annotation { "Feature Type Name" : "Feature", "Feature Type Description" : "" }
export const myFeature = defineFeature(function(context is Context, id is Id, definition is map)
    precondition{}
    {
        {
            var Q0;
            Q0=qCreatedBy(makeId("Front.planeOp"),FACE);
            var sketch = newSketch(context, id + "F0", { "sketchPlane" : qUnion([Q0])});
            skLineSegment(sketch, "E0.bottom", {"start": v(-25.4, 12.7) * mm, "end": v(25.4, 12.7) * mm});
            skLineSegment(sketch, "E0.top", {"start": v(-25.4, 0) * mm, "end": v(25.4, 0) * mm});
            skLineSegment(sketch, "E0.left", {"start": v(-25.4, 12.7) * mm, "end": v(-25.4, 0) * mm});
            skLineSegment(sketch, "E0.right", {"start": v(25.4, 12.7) * mm, "end": v(25.4, 0) * mm});
            skLineSegment(sketch, "E1", {"start": v(-25.4, 12.7) * mm, "end": v(0, 19.05) * mm});
            skLineSegment(sketch, "E2", {"start": v(0, 19.05) * mm, "end": v(25.4, 12.7) * mm});
            skSolve(sketch);
        }
        {
            var Q0;
            Q0=makeQuery(id+"F0.imprint","IMPRINT",FACE,{"disambiguationData":[TD([[makeQuery(id+"F0.imprint","IMPRINT",EDGE,{"derivedFrom":sQuery(id+"F0.wireOp",EDGE,"E0.bottom")}),-1.0]])]});
            var Q1;
            Q1=makeQuery(id+"F0.imprint","IMPRINT",FACE,{"disambiguationData":[TD([[makeQuery(id+"F0.imprint","IMPRINT",EDGE,{"derivedFrom":sQuery(id+"F0.wireOp",EDGE,"E0.bottom")}),1.0]])]});
            extrude(context, id + "F1", {"entities" : qUnion([Q0, Q1]), "depth" : 57.15 * mm});
        }
        {
            var Q0;
            Q0=makeQuery(id+"F1.opExtrude","CAP_FACE",FACE,{"disambiguationData":[OSD([sQuery(id+"F0.wireOp",EDGE,"E0.top"),sQuery(id+"F0.wireOp",EDGE,"E0.left"),sQuery(id+"F0.wireOp",EDGE,"E0.right"),sQuery(id+"F0.wireOp",EDGE,"E1"),sQuery(id+"F0.wireOp",EDGE,"E2")])],"isStart":false});
            var sketch = newSketch(context, id + "F2", { "sketchPlane" : qUnion([Q0])});
            skLineSegment(sketch, "E3.bottom", {"start": v(-9.53, 0) * mm, "end": v(9.53, 0) * mm});
            skLineSegment(sketch, "E3.top", {"start": v(-9.53, 11.11) * mm, "end": v(9.52, 11.11) * mm});
            skLineSegment(sketch, "E3.left", {"start": v(-9.53, 0) * mm, "end": v(-9.53, 11.11) * mm});
            skLineSegment(sketch, "E3.right", {"start": v(9.53, 0) * mm, "end": v(9.52, 11.11) * mm});
            skLineSegment(sketch, "E4.bottom", {"start": v(-19.05, 0) * mm, "end": v(-15.88, 0) * mm});
            skLineSegment(sketch, "E4.top", {"start": v(-19.05, 6.35) * mm, "end": v(-15.88, 6.35) * mm});
            skLineSegment(sketch, "E4.left", {"start": v(-19.05, 0) * mm, "end": v(-19.05, 6.35) * mm});
            skLineSegment(sketch, "E4.right", {"start": v(-15.88, 0) * mm, "end": v(-15.88, 6.35) * mm});
            skSolve(sketch);
        }
        {
            var Q0;
            Q0=makeQuery(id+"F2.imprint","IMPRINT",FACE,{"disambiguationData":[TD([[makeQuery(id+"F2.imprint","IMPRINT",EDGE,{"derivedFrom":sQuery(id+"F2.wireOp",EDGE,"E3.bottom")}),1.0]])]});
            extrude(context, id + "F3", {"entities" : qUnion([Q0]), "operationType" : NewBodyOperationType.REMOVE, "oppositeDirection" : true, "depth" : 1.27 * mm});
        }
        {
            var Q0;
            Q0=makeQuery(id+"F3.boolean.opBoolean","COPY",FACE,{"derivedFrom":makeQuery(id+"F3.opExtrude","CAP_FACE",FACE,{"disambiguationData":[OSD([sQuery(id+"F2.wireOp",EDGE,"E3.bottom"),sQuery(id+"F2.wireOp",EDGE,"E3.top"),sQuery(id+"F2.wireOp",EDGE,"E3.left"),sQuery(id+"F2.wireOp",EDGE,"E3.right")])],"isStart":false})});
            var sketch = newSketch(context, id + "F4", { "sketchPlane" : qUnion([Q0])});
            skLineSegment(sketch, "E5", {"start": v(-8.5, 0) * mm, "end": v(-8.5, 10.1) * mm});
            skLineSegment(sketch, "E6", {"start": v(-8.5, 10.1) * mm, "end": v(-1.14, 10.1) * mm});
            skLineSegment(sketch, "E7", {"start": v(-1.14, 10.1) * mm, "end": v(-1.14, 0) * mm});
            skLineSegment(sketch, "E8", {"start": v(-1.14, 0) * mm, "end": v(-0.13, 0) * mm});
            skLineSegment(sketch, "E9", {"start": v(-0.13, 0) * mm, "end": v(-0.13, 11.11) * mm});
            skLineSegment(sketch, "E10", {"start": v(-8.5, 6.1) * mm, "end": v(-1.14, 6.1) * mm});
            skLineSegment(sketch, "E11", {"start": v(-8.5, 5.08) * mm, "end": v(-1.14, 5.08) * mm});
            skLineSegment(sketch, "E12", {"start": v(-8.5, 1.02) * mm, "end": v(-1.14, 1.02) * mm});
            skLineSegment(sketch, "E13", {"start": v(-1.14, 5.08) * mm, "end": v(-8.5, 1.02) * mm});
            skLineSegment(sketch, "E14", {"start": v(-2.2, 5.08) * mm, "end": v(-8.5, 1.6) * mm});
            skLineSegment(sketch, "E15", {"start": v(-1.14, 4.5) * mm, "end": v(-7.46, 1.02) * mm});
            skLineSegment(sketch, "E16", {"start": v(-0.13, 11.11) * mm, "end": v(-9.53, 11.11) * mm});
            skLineSegment(sketch, "E17", {"start": v(-9.53, 11.11) * mm, "end": v(-9.53, 0) * mm});
            skLineSegment(sketch, "E18", {"start": v(-9.53, 0) * mm, "end": v(-0.13, 0) * mm});
            skLineSegment(sketch, "E19.MirrorCS", {"start": v(1.14, 5.08) * mm, "end": v(8.5, 1.02) * mm});
            skLineSegment(sketch, "E20.MirrorCS", {"start": v(1.14, 10.1) * mm, "end": v(1.14, 0) * mm});
            skLineSegment(sketch, "E21.MirrorCS", {"start": v(8.5, 6.1) * mm, "end": v(1.14, 6.1) * mm});
            skLineSegment(sketch, "E22.MirrorCS", {"start": v(8.5, 5.08) * mm, "end": v(1.14, 5.08) * mm});
            skLineSegment(sketch, "E23.MirrorCS", {"start": v(2.2, 5.08) * mm, "end": v(8.5, 1.6) * mm});
            skLineSegment(sketch, "E24.MirrorCS", {"start": v(1.14, 4.5) * mm, "end": v(7.46, 1.02) * mm});
            skLineSegment(sketch, "E25.MirrorCS", {"start": v(8.5, 1.02) * mm, "end": v(1.14, 1.02) * mm});
            skLineSegment(sketch, "E26.MirrorCS", {"start": v(9.53, 0) * mm, "end": v(0.13, 0) * mm});
            skLineSegment(sketch, "E27.MirrorCS", {"start": v(8.5, 0) * mm, "end": v(8.5, 10.1) * mm});
            skLineSegment(sketch, "E28.MirrorCS", {"start": v(9.53, 11.11) * mm, "end": v(9.53, 0) * mm});
            skLineSegment(sketch, "E29.MirrorCS", {"start": v(8.5, 10.1) * mm, "end": v(1.14, 10.1) * mm});
            skLineSegment(sketch, "E30.MirrorCS", {"start": v(0.13, 11.11) * mm, "end": v(9.53, 11.11) * mm});
            skLineSegment(sketch, "E31.MirrorCS", {"start": v(0.13, 0) * mm, "end": v(0.13, 11.11) * mm});
            skSolve(sketch);
        }
        {
            var Q0;
            {var subQ9=sQuery(id+"F4.wireOp",EDGE,"E6");Q0=makeQuery(id+"F4.imprint","IMPRINT",FACE,{"disambiguationData":[TD([[makeQuery(id+"F4.imprint","IMPRINT",EDGE,{"derivedFrom":subQ9}),1.0]])]});}
            var Q1;
            {var subQ4=sQuery(id+"F4.wireOp",EDGE,"E10");Q1=makeQuery(id+"F4.imprint","IMPRINT",FACE,{"disambiguationData":[TD([[makeQuery(id+"F4.imprint","IMPRINT",EDGE,{"derivedFrom":subQ4}),-1.0]])]});}
            var Q2;
            {var subQ0=sQuery(id+"F4.wireOp",EDGE,"E13");Q2=makeQuery(id+"F4.imprint","IMPRINT",FACE,{"disambiguationData":[TD([[makeQuery(id+"F4.imprint","IMPRINT",EDGE,{"derivedFrom":subQ0}),-1.0]])]});}
            var Q3;
            {var subQ0=sQuery(id+"F4.wireOp",EDGE,"E13");Q3=makeQuery(id+"F4.imprint","IMPRINT",FACE,{"disambiguationData":[TD([[makeQuery(id+"F4.imprint","IMPRINT",EDGE,{"derivedFrom":subQ0}),1.0]])]});}
            var Q4;
            {var subQ1=sQuery(id+"F4.wireOp",EDGE,"E7");var subQ6=sQuery(id+"F4.wireOp",EDGE,"E18");var subQ8=makeQuery(id+"F4.imprint","INTERSECT",VERTEX,{"derivedFrom":[subQ1,subQ6]});Q4=makeQuery(id+"F4.imprint","IMPRINT",FACE,{"disambiguationData":[TD([[makeQuery(id+"F4.imprint","IMPRINT",EDGE,{"disambiguationData":[TD([[subQ8,1.0]])],"derivedFrom":subQ1}),-1.0]])]});}
            var Q5;
            {var subQ2=sQuery(id+"F4.wireOp",EDGE,"E20.MirrorCS");var subQ4=sQuery(id+"F4.wireOp",EDGE,"E26.MirrorCS");var subQ5=makeQuery(id+"F4.imprint","INTERSECT",VERTEX,{"derivedFrom":[subQ2,subQ4]});Q5=makeQuery(id+"F4.imprint","IMPRINT",FACE,{"disambiguationData":[TD([[makeQuery(id+"F4.imprint","IMPRINT",EDGE,{"disambiguationData":[TD([[subQ5,1.0]])],"derivedFrom":subQ2}),1.0]])]});}
            var Q6;
            {var subQ17=sQuery(id+"F4.wireOp",EDGE,"E28.MirrorCS");Q6=makeQuery(id+"F4.imprint","IMPRINT",FACE,{"disambiguationData":[TD([[makeQuery(id+"F4.imprint","IMPRINT",EDGE,{"derivedFrom":subQ17}),1.0]])]});}
            var Q7;
            {var subQ4=sQuery(id+"F4.wireOp",EDGE,"E21.MirrorCS");Q7=makeQuery(id+"F4.imprint","IMPRINT",FACE,{"disambiguationData":[TD([[makeQuery(id+"F4.imprint","IMPRINT",EDGE,{"derivedFrom":subQ4}),1.0]])]});}
            var Q8;
            {var subQ0=sQuery(id+"F4.wireOp",EDGE,"E19.MirrorCS");Q8=makeQuery(id+"F4.imprint","IMPRINT",FACE,{"disambiguationData":[TD([[makeQuery(id+"F4.imprint","IMPRINT",EDGE,{"derivedFrom":subQ0}),1.0]])]});}
            var Q9;
            {var subQ0=sQuery(id+"F4.wireOp",EDGE,"E19.MirrorCS");Q9=makeQuery(id+"F4.imprint","IMPRINT",FACE,{"disambiguationData":[TD([[makeQuery(id+"F4.imprint","IMPRINT",EDGE,{"derivedFrom":subQ0}),-1.0]])]});}
            extrude(context, id + "F5", {"entities" : qUnion([Q0, Q1, Q2, Q3, Q4, Q5, Q6, Q7, Q8, Q9]), "operationType" : NewBodyOperationType.ADD, "depth" : 0.64 * mm});
        }
        {
            var Q0;
            {var subQ0=sQuery(id+"F0.wireOp",EDGE,"E0.left");var subQ1=sQuery(id+"F0.wireOp",EDGE,"E1");var subQ2=sQuery(id+"F0.wireOp",EDGE,"E2");var subQ3=sQuery(id+"F0.wireOp",EDGE,"E0.right");var subQ4=sQuery(id+"F0.wireOp",EDGE,"E0.top");Q0=makeQuery(id+"FkIv4KLba7RXvQa_1.boolean.opBoolean","SPLIT",FACE,{"disambiguationData":[TD([makeQuery(id+"F1.opExtrude","SWEPT_FACE",FACE,{"disambiguationData":[OSD([subQ4])]})])],"derivedFrom":makeQuery(id+"F1.opExtrude","CAP_FACE",FACE,{"disambiguationData":[OSD([subQ4,subQ0,subQ3,subQ1,subQ2])],"isStart":false})});}
            var sketch = newSketch(context, id + "F6", { "sketchPlane" : qUnion([Q0])});
            skLineSegment(sketch, "E32.bottom", {"start": v(-19.05, 0) * mm, "end": v(-15.88, 0) * mm});
            skLineSegment(sketch, "E32.top", {"start": v(-19.05, 6.35) * mm, "end": v(-15.88, 6.35) * mm});
            skLineSegment(sketch, "E32.left", {"start": v(-19.05, 0) * mm, "end": v(-19.05, 6.35) * mm});
            skLineSegment(sketch, "E32.right", {"start": v(-15.88, 0) * mm, "end": v(-15.88, 6.35) * mm});
            skSolve(sketch);
        }
        {
            var Q0;
            Q0=makeQuery(id+"F6.imprint","IMPRINT",FACE,{"disambiguationData":[TD([[makeQuery(id+"F6.imprint","IMPRINT",EDGE,{"derivedFrom":sQuery(id+"F6.wireOp",EDGE,"E32.bottom")}),1.0]])]});
            extrude(context, id + "F7", {"entities" : qUnion([Q0]), "operationType" : NewBodyOperationType.REMOVE, "oppositeDirection" : true, "depth" : 0.5 * mm});
        }
        {
            var Q0;
            Q0=makeQuery(id+"F7.boolean.opBoolean","COPY",FACE,{"derivedFrom":makeQuery(id+"F7.opExtrude","CAP_FACE",FACE,{"disambiguationData":[OSD([sQuery(id+"F6.wireOp",EDGE,"E32.bottom"),sQuery(id+"F6.wireOp",EDGE,"E32.top"),sQuery(id+"F6.wireOp",EDGE,"E32.left"),sQuery(id+"F6.wireOp",EDGE,"E32.right")])],"isStart":false})});
            var sketch = newSketch(context, id + "F8", { "sketchPlane" : qUnion([Q0])});
            skCircle(sketch, "E33", {"center": v(-18.29, 3.18) * mm, "radius": 0.2 * mm});
            skSolve(sketch);
        }
        {
            var Q0;
            Q0=makeQuery(id+"F8.imprint","IMPRINT",FACE,{"disambiguationData":[TD([[makeQuery(id+"F8.imprint","IMPRINT",EDGE,{"derivedFrom":sQuery(id+"F8.wireOp",EDGE,"E33")}),1.0]])]});
            extrude(context, id + "F9", {"entities" : qUnion([Q0]), "operationType" : NewBodyOperationType.ADD, "depth" : 0.5 * mm});
        }
        {
            var Q0;
            Q0=makeQuery(id+"F1.opExtrude","SWEPT_FACE",FACE,{"disambiguationData":[OSD([sQuery(id+"F0.wireOp",EDGE,"E0.left")])]});
            var sketch = newSketch(context, id + "F10", { "sketchPlane" : qUnion([Q0])});
            skLineSegment(sketch, "E34.bottom", {"start": v(53.97, 9.52) * mm, "end": v(41.37, 9.52) * mm});
            skLineSegment(sketch, "E34.top", {"start": v(53.97, 2.54) * mm, "end": v(41.37, 2.54) * mm});
            skLineSegment(sketch, "E34.left", {"start": v(53.97, 9.52) * mm, "end": v(53.97, 2.54) * mm});
            skLineSegment(sketch, "E34.right", {"start": v(41.37, 9.52) * mm, "end": v(41.37, 2.54) * mm});
            skLineSegment(sketch, "E35.bottom", {"start": v(40.35, 9.53) * mm, "end": v(27.75, 9.53) * mm});
            skLineSegment(sketch, "E35.top", {"start": v(40.35, 2.54) * mm, "end": v(27.75, 2.54) * mm});
            skLineSegment(sketch, "E35.left", {"start": v(40.35, 9.53) * mm, "end": v(40.35, 2.54) * mm});
            skLineSegment(sketch, "E35.right", {"start": v(27.75, 9.53) * mm, "end": v(27.75, 2.54) * mm});
            skLineSegment(sketch, "E36.bottom", {"start": v(26.73, 9.52) * mm, "end": v(14.13, 9.52) * mm});
            skLineSegment(sketch, "E36.top", {"start": v(26.73, 2.54) * mm, "end": v(14.13, 2.54) * mm});
            skLineSegment(sketch, "E36.left", {"start": v(26.73, 9.53) * mm, "end": v(26.73, 2.54) * mm});
            skLineSegment(sketch, "E36.right", {"start": v(14.13, 9.53) * mm, "end": v(14.13, 2.54) * mm});
            skLineSegment(sketch, "E37.bottom", {"start": v(13.11, 9.52) * mm, "end": v(0.5, 9.52) * mm});
            skLineSegment(sketch, "E37.top", {"start": v(13.11, 2.54) * mm, "end": v(0.5, 2.54) * mm});
            skLineSegment(sketch, "E37.left", {"start": v(13.11, 9.52) * mm, "end": v(13.11, 2.54) * mm});
            skLineSegment(sketch, "E37.right", {"start": v(0.5, 9.52) * mm, "end": v(0.5, 2.54) * mm});
            skSolve(sketch);
        }
        {
            var Q0;
            Q0=makeQuery(id+"F10.imprint","IMPRINT",FACE,{"disambiguationData":[TD([[makeQuery(id+"F10.imprint","IMPRINT",EDGE,{"derivedFrom":sQuery(id+"F10.wireOp",EDGE,"727a1d76-4258-429a-ad4e-49e237d1b87a.bottom")}),1.0]])]});
            var Q1;
            Q1=makeQuery(id+"F10.imprint","IMPRINT",FACE,{"disambiguationData":[TD([[makeQuery(id+"F10.imprint","IMPRINT",EDGE,{"derivedFrom":sQuery(id+"F10.wireOp",EDGE,"fbcd54c6-16bd-4673-946f-ba1503210179.bottom")}),1.0]])]});
            var Q2;
            Q2=makeQuery(id+"F10.imprint","IMPRINT",FACE,{"disambiguationData":[TD([[makeQuery(id+"F10.imprint","IMPRINT",EDGE,{"derivedFrom":sQuery(id+"F10.wireOp",EDGE,"f456708e-a3c8-40d2-a44c-2f1cd61e3648.bottom")}),1.0]])]});
            var Q3;
            Q3=makeQuery(id+"F10.imprint","IMPRINT",FACE,{"disambiguationData":[TD([[makeQuery(id+"F10.imprint","IMPRINT",EDGE,{"derivedFrom":sQuery(id+"F10.wireOp",EDGE,"857afa44-62f5-48bd-8139-67d137270524.bottom")}),1.0]])]});
            var Q4;
            Q4=makeQuery(id+"F10.imprint","IMPRINT",FACE,{"disambiguationData":[TD([[makeQuery(id+"F10.imprint","IMPRINT",EDGE,{"derivedFrom":sQuery(id+"F10.wireOp",EDGE,"E37.bottom")}),1.0]])]});
            var Q5;
            Q5=makeQuery(id+"F10.imprint","IMPRINT",FACE,{"disambiguationData":[TD([[makeQuery(id+"F10.imprint","IMPRINT",EDGE,{"derivedFrom":sQuery(id+"F10.wireOp",EDGE,"E36.bottom")}),1.0]])]});
            var Q6;
            Q6=makeQuery(id+"F10.imprint","IMPRINT",FACE,{"disambiguationData":[TD([[makeQuery(id+"F10.imprint","IMPRINT",EDGE,{"derivedFrom":sQuery(id+"F10.wireOp",EDGE,"E35.bottom")}),1.0]])]});
            var Q7;
            Q7=makeQuery(id+"F10.imprint","IMPRINT",FACE,{"disambiguationData":[TD([[makeQuery(id+"F10.imprint","IMPRINT",EDGE,{"derivedFrom":sQuery(id+"F10.wireOp",EDGE,"E34.bottom")}),1.0]])]});
            extrude(context, id + "F11", {"entities" : qUnion([Q0, Q1, Q2, Q3, Q4, Q5, Q6, Q7]), "operationType" : NewBodyOperationType.REMOVE, "oppositeDirection" : true, "depth" : 0.38 * mm});
        }
        {
            var Q0;
            Q0=makeQuery(id+"F1.opExtrude","SWEPT_FACE",FACE,{"disambiguationData":[OSD([sQuery(id+"F0.wireOp",EDGE,"E0.right")])]});
            var sketch = newSketch(context, id + "F12", { "sketchPlane" : qUnion([Q0])});
            skLineSegment(sketch, "E38.bottom", {"start": v(-53.98, 9.53) * mm, "end": v(-41.37, 9.53) * mm});
            skLineSegment(sketch, "E38.top", {"start": v(-53.98, 2.54) * mm, "end": v(-41.37, 2.54) * mm});
            skLineSegment(sketch, "E38.left", {"start": v(-53.98, 9.53) * mm, "end": v(-53.98, 2.54) * mm});
            skLineSegment(sketch, "E38.right", {"start": v(-41.37, 9.53) * mm, "end": v(-41.37, 2.54) * mm});
            skLineSegment(sketch, "E39.bottom", {"start": v(-40.35, 9.53) * mm, "end": v(-27.75, 9.53) * mm});
            skLineSegment(sketch, "E39.top", {"start": v(-40.35, 2.54) * mm, "end": v(-27.75, 2.54) * mm});
            skLineSegment(sketch, "E39.left", {"start": v(-40.35, 9.53) * mm, "end": v(-40.35, 2.54) * mm});
            skLineSegment(sketch, "E39.right", {"start": v(-27.75, 9.53) * mm, "end": v(-27.75, 2.54) * mm});
            skLineSegment(sketch, "E40.bottom", {"start": v(-26.73, 9.53) * mm, "end": v(-14.13, 9.53) * mm});
            skLineSegment(sketch, "E40.top", {"start": v(-26.73, 2.54) * mm, "end": v(-14.13, 2.54) * mm});
            skLineSegment(sketch, "E40.left", {"start": v(-26.73, 9.53) * mm, "end": v(-26.73, 2.54) * mm});
            skLineSegment(sketch, "E40.right", {"start": v(-14.13, 9.53) * mm, "end": v(-14.13, 2.54) * mm});
            skLineSegment(sketch, "E41.bottom", {"start": v(-13.11, 9.53) * mm, "end": v(-0.5, 9.53) * mm});
            skLineSegment(sketch, "E41.top", {"start": v(-13.11, 2.54) * mm, "end": v(-0.5, 2.54) * mm});
            skLineSegment(sketch, "E41.left", {"start": v(-13.11, 9.53) * mm, "end": v(-13.11, 2.54) * mm});
            skLineSegment(sketch, "E41.right", {"start": v(-0.5, 9.53) * mm, "end": v(-0.5, 2.54) * mm});
            skSolve(sketch);
        }
        {
            var Q0;
            Q0=makeQuery(id+"F12.imprint","IMPRINT",FACE,{"disambiguationData":[TD([[makeQuery(id+"F12.imprint","IMPRINT",EDGE,{"derivedFrom":sQuery(id+"F12.wireOp",EDGE,"E38.bottom")}),-1.0]])]});
            var Q1;
            Q1=makeQuery(id+"F12.imprint","IMPRINT",FACE,{"disambiguationData":[TD([[makeQuery(id+"F12.imprint","IMPRINT",EDGE,{"derivedFrom":sQuery(id+"F12.wireOp",EDGE,"E39.bottom")}),-1.0]])]});
            var Q2;
            Q2=makeQuery(id+"F12.imprint","IMPRINT",FACE,{"disambiguationData":[TD([[makeQuery(id+"F12.imprint","IMPRINT",EDGE,{"derivedFrom":sQuery(id+"F12.wireOp",EDGE,"E40.bottom")}),-1.0]])]});
            var Q3;
            Q3=makeQuery(id+"F12.imprint","IMPRINT",FACE,{"disambiguationData":[TD([[makeQuery(id+"F12.imprint","IMPRINT",EDGE,{"derivedFrom":sQuery(id+"F12.wireOp",EDGE,"E41.bottom")}),-1.0]])]});
            var Q4;
            Q4=makeQuery(id+"F12.imprint","IMPRINT",FACE,{"disambiguationData":[TD([[makeQuery(id+"F12.imprint","IMPRINT",EDGE,{"derivedFrom":sQuery(id+"F12.wireOp",EDGE,"e12e58a7-e691-4093-903c-9c184ae4cd88.bottom")}),-1.0]])]});
            var Q5;
            Q5=makeQuery(id+"F12.imprint","IMPRINT",FACE,{"disambiguationData":[TD([[makeQuery(id+"F12.imprint","IMPRINT",EDGE,{"derivedFrom":sQuery(id+"F12.wireOp",EDGE,"4a9eed8a-eaee-461f-81b4-e3a02307e155.bottom")}),-1.0]])]});
            var Q6;
            Q6=makeQuery(id+"F12.imprint","IMPRINT",FACE,{"disambiguationData":[TD([[makeQuery(id+"F12.imprint","IMPRINT",EDGE,{"derivedFrom":sQuery(id+"F12.wireOp",EDGE,"bde78560-5837-450a-b62f-a72f43ab685d.bottom")}),-1.0]])]});
            var Q7;
            Q7=makeQuery(id+"F12.imprint","IMPRINT",FACE,{"disambiguationData":[TD([[makeQuery(id+"F12.imprint","IMPRINT",EDGE,{"derivedFrom":sQuery(id+"F12.wireOp",EDGE,"723e41c7-2ad6-4fed-aca1-4fab76280504.bottom")}),-1.0]])]});
            extrude(context, id + "F13", {"entities" : qUnion([Q0, Q1, Q2, Q3, Q4, Q5, Q6, Q7]), "operationType" : NewBodyOperationType.REMOVE, "oppositeDirection" : true, "depth" : 0.38 * mm});
        }
        {
            var Q0;
            Q0=makeQuery(id+"F1.opExtrude","SWEPT_BODY",BODY,{"disambiguationData":[OSD([sQuery(id+"F0.wireOp",EDGE,"E0.top"),sQuery(id+"F0.wireOp",EDGE,"E0.left"),sQuery(id+"F0.wireOp",EDGE,"E0.right"),sQuery(id+"F0.wireOp",EDGE,"E1"),sQuery(id+"F0.wireOp",EDGE,"E2")])]});
            var Q1;
            Q1=qCreatedBy(makeId("Front.planeOp"),FACE);
            mirror(context, id + "F14", {"operationType" : NewBodyOperationType.ADD, "entities" : qUnion([Q0]), "mirrorPlane" : qUnion([Q1])});
        }
        {
            var Q0;
            Q0=makeQuery(id+"F1.opExtrude","CAP_FACE",FACE,{"disambiguationData":[OSD([sQuery(id+"F0.wireOp",EDGE,"E0.top"),sQuery(id+"F0.wireOp",EDGE,"E0.left"),sQuery(id+"F0.wireOp",EDGE,"E0.right"),sQuery(id+"F0.wireOp",EDGE,"E1"),sQuery(id+"F0.wireOp",EDGE,"E2")])],"isStart":false});
            var sketch = newSketch(context, id + "F15", { "sketchPlane" : qUnion([Q0])});
            skText(sketch, "E42", { "text": "Achen Farms", "fontName": "OpenSans-Regular.ttf"});
            const initialGuessF15  = {"E42": [-0.01323, 0.01207, 1, 0, 0.00317]};
            skSetInitialGuess(sketch, initialGuessF15);
            skSolve(sketch);
        }
        {
            var Q0;
            Q0 = qSketchRegion(id + "F15", true);
            extrude(context, id + "F16", {"entities" : qUnion([Q0]), "operationType" : NewBodyOperationType.REMOVE, "oppositeDirection" : true, "depth" : 0.38 * mm});
        }
        {
            var Q0;
            Q0=makeQuery(id+"F14.opPattern","COPY",FACE,{"derivedFrom":makeQuery(id+"F1.opExtrude","CAP_FACE",FACE,{"disambiguationData":[OSD([sQuery(id+"F0.wireOp",EDGE,"E0.top"),sQuery(id+"F0.wireOp",EDGE,"E0.left"),sQuery(id+"F0.wireOp",EDGE,"E0.right"),sQuery(id+"F0.wireOp",EDGE,"E1"),sQuery(id+"F0.wireOp",EDGE,"E2")])],"isStart":false}),"instanceName":"1"});
            var sketch = newSketch(context, id + "F17", { "sketchPlane" : qUnion([Q0])});
            skText(sketch, "E43", { "text": "Achen Farms", "fontName": "OpenSans-Regular.ttf"});
            const initialGuessF17  = {"E43": [-0.01323, 0.01206, 1, 0, 0.00318]};
            skSetInitialGuess(sketch, initialGuessF17);
            skSolve(sketch);
        }
        {
            var Q0;
            Q0 = qSketchRegion(id + "F17", true);
            extrude(context, id + "F18", {"entities" : qUnion([Q0]), "operationType" : NewBodyOperationType.REMOVE, "oppositeDirection" : true, "depth" : 0.38 * mm});
        }
        {
            var Q0;
            {var subQ0=makeQuery(id+"F5.boolean.opBoolean","MERGE",FACE,{"derivedFrom":[makeQuery(id+"F1.opExtrude","SWEPT_FACE",FACE,{"disambiguationData":[OSD([sQuery(id+"F0.wireOp",EDGE,"E0.top")])]}),makeQuery(id+"F5.opExtrude","SWEPT_FACE",FACE,{"disambiguationData":[OSD([sQuery(id+"F4.wireOp",EDGE,"E18")])]}),makeQuery(id+"F5.opExtrude","SWEPT_FACE",FACE,{"disambiguationData":[OSD([sQuery(id+"F4.wireOp",EDGE,"E26.MirrorCS")])]})]});Q0=makeQuery(id+"F14.boolean.opBoolean","MERGE",FACE,{"derivedFrom":[subQ0,makeQuery(id+"F14.opPattern","COPY",FACE,{"derivedFrom":subQ0,"instanceName":"1"})]});}
            var sketch = newSketch(context, id + "F19", { "sketchPlane" : qUnion([Q0])});
            skLineSegment(sketch, "E44.bottom", {"start": v(-25.4, 57.15) * mm, "end": v(-36.51, 57.15) * mm});
            skLineSegment(sketch, "E44.top", {"start": v(-25.4, 47.63) * mm, "end": v(-36.51, 47.63) * mm});
            skLineSegment(sketch, "E44.left", {"start": v(-25.4, 57.15) * mm, "end": v(-25.4, 47.63) * mm});
            skLineSegment(sketch, "E44.right", {"start": v(-36.51, 57.15) * mm, "end": v(-36.51, 47.62) * mm});
            skSolve(sketch);
        }
        {
            var Q0;
            Q0=makeQuery(id+"F19.imprint","IMPRINT",FACE,{"disambiguationData":[TD([[makeQuery(id+"F19.imprint","IMPRINT",EDGE,{"derivedFrom":sQuery(id+"F19.wireOp",EDGE,"E44.bottom")}),1.0]])]});
            extrude(context, id + "F20", {"entities" : qUnion([Q0]), "operationType" : NewBodyOperationType.ADD, "oppositeDirection" : true, "depth" : 0.64 * mm});
        }
        {
            var Q0;
            {var subQ0=sQuery(id+"F0.wireOp",EDGE,"E0.right");var subQ4=sQuery(id+"F0.wireOp",EDGE,"E0.top");var subQ5=makeQuery(id+"F1.opExtrude","SWEPT_FACE",FACE,{"disambiguationData":[OSD([subQ4])]});var subQ6=sQuery(id+"F0.wireOp",EDGE,"E0.left");var subQ8=sQuery(id+"F0.wireOp",EDGE,"E1");var subQ10=sQuery(id+"F0.wireOp",EDGE,"E2");Q0=makeQuery(id+"F20.boolean.opBoolean","MERGE",FACE,{"derivedFrom":[makeQuery(id+"F16.boolean.opBoolean","SPLIT",FACE,{"disambiguationData":[TD([subQ5])],"derivedFrom":makeQuery(id+"F1.opExtrude","CAP_FACE",FACE,{"disambiguationData":[OSD([subQ4,subQ6,subQ0,subQ8,subQ10])],"isStart":false})}),makeQuery(id+"F20.opExtrude","SWEPT_FACE",FACE,{"disambiguationData":[OSD([sQuery(id+"F19.wireOp",EDGE,"E44.bottom")])]})]});}
            cPlane(context, id + "F21", {"entities" : qUnion([Q0]), "cplaneType" : CPlaneType.OFFSET, "offset" : 4.76 * mm, "oppositeDirection" : true, "width" : 152.4 * mm, "height" : 152.4 * mm});
        }
        {
            var Q0;
            Q0=qCreatedBy(id+"F21.planeOp",FACE);
            var sketch = newSketch(context, id + "F22", { "sketchPlane" : qUnion([Q0])});
            skLineSegment(sketch, "E45", {"start": v(-33.02, 0.64) * mm, "end": v(-36.2, 5.17) * mm});
            skLineSegment(sketch, "E46", {"start": v(-36.2, 5.17) * mm, "end": v(-36.2, 15.88) * mm});
            skLineSegment(sketch, "E47", {"start": v(-36.2, 15.88) * mm, "end": v(-33.15, 16.7) * mm});
            skLineSegment(sketch, "E48", {"start": v(-33.15, 16.7) * mm, "end": v(-33.15, 17.14) * mm});
            skLineSegment(sketch, "E49", {"start": v(-33.15, 17.14) * mm, "end": v(-33.65, 17.14) * mm});
            skLineSegment(sketch, "E50", {"start": v(-33.65, 17.14) * mm, "end": v(-33.65, 17.65) * mm});
            skLineSegment(sketch, "E51", {"start": v(-33.65, 17.65) * mm, "end": v(-31.75, 17.65) * mm});
            skLineSegment(sketch, "E52", {"start": v(-33.02, 0.64) * mm, "end": v(-31.75, 0.64) * mm});
            skLineSegment(sketch, "E53", {"start": v(-31.75, 0.64) * mm, "end": v(-31.75, 17.65) * mm});
            skSolve(sketch);
        }
        {
            var Q0;
            Q0=makeQuery(id+"F22.imprint","IMPRINT",FACE,{"disambiguationData":[TD([[makeQuery(id+"F22.imprint","IMPRINT",EDGE,{"derivedFrom":sQuery(id+"F22.wireOp",EDGE,"E45")}),-1.0]])]});
            var Q1;
            Q1=sQuery(id+"F22.wireOp",EDGE,"E53");
            revolve(context, id + "F23", {"operationType" : NewBodyOperationType.ADD, "entities" : qUnion([Q0]), "axis" : qUnion([Q1]), "revolveType" : RevolveType.FULL});
        }
        {
            var Q0;
            Q0=makeQuery(id+"F20.opExtrude","CAP_FACE",FACE,{"disambiguationData":[OSD([sQuery(id+"F19.wireOp",EDGE,"E44.bottom"),sQuery(id+"F19.wireOp",EDGE,"E44.top"),sQuery(id+"F19.wireOp",EDGE,"E44.left"),sQuery(id+"F19.wireOp",EDGE,"E44.right")])],"isStart":false});
            var sketch = newSketch(context, id + "F24", { "sketchPlane" : qUnion([Q0])});
            skCircle(sketch, "E54", {"center": v(-31.75, -52.39) * mm, "radius": 4.45 * mm, "construction": true});
            skCircle(sketch, "E55", {"center": v(-34.52, -49.6) * mm, "radius": 0.5 * mm});
            skCircle(sketch, "E56", {"center": v(-31.75, -52.39) * mm, "radius": 3.94 * mm, "construction": true});
            skCircle(sketch, "E57", {"center": v(-28.98, -49.6) * mm, "radius": 0.5 * mm});
            skCircle(sketch, "E58", {"center": v(-34.52, -55.18) * mm, "radius": 0.5 * mm});
            skCircle(sketch, "E59", {"center": v(-28.98, -55.18) * mm, "radius": 0.5 * mm});
            skLineSegment(sketch, "E60", {"start": v(-34.52, -49.6) * mm, "end": v(-34.52, -55.18) * mm, "construction": true});
            skLineSegment(sketch, "E61", {"start": v(-28.98, -55.18) * mm, "end": v(-34.52, -55.18) * mm, "construction": true});
            skLineSegment(sketch, "E62", {"start": v(-28.98, -55.18) * mm, "end": v(-28.98, -49.6) * mm, "construction": true});
            skLineSegment(sketch, "E63", {"start": v(-28.98, -49.6) * mm, "end": v(-34.52, -49.6) * mm, "construction": true});
            skSolve(sketch);
        }
        {
            var Q0;
            Q0=makeQuery(id+"F24.imprint","IMPRINT",FACE,{"disambiguationData":[TD([[makeQuery(id+"F24.imprint","IMPRINT",EDGE,{"derivedFrom":sQuery(id+"F24.wireOp",EDGE,"E58")}),1.0]])]});
            var Q1;
            Q1=makeQuery(id+"F24.imprint","IMPRINT",FACE,{"disambiguationData":[TD([[makeQuery(id+"F24.imprint","IMPRINT",EDGE,{"derivedFrom":sQuery(id+"F24.wireOp",EDGE,"E59")}),1.0]])]});
            var Q2;
            Q2=makeQuery(id+"F24.imprint","IMPRINT",FACE,{"disambiguationData":[TD([[makeQuery(id+"F24.imprint","IMPRINT",EDGE,{"derivedFrom":sQuery(id+"F24.wireOp",EDGE,"E55")}),1.0]])]});
            var Q3;
            Q3=makeQuery(id+"F24.imprint","IMPRINT",FACE,{"disambiguationData":[TD([[makeQuery(id+"F24.imprint","IMPRINT",EDGE,{"derivedFrom":sQuery(id+"F24.wireOp",EDGE,"E57")}),1.0]])]});
            extrude(context, id + "F25", {"entities" : qUnion([Q0, Q1, Q2, Q3]), "operationType" : NewBodyOperationType.ADD, "depth" : 12.7 * mm});
        }
        {
            var Q0;
            Q0=makeQuery(id+"F20.opExtrude","SWEPT_EDGE",EDGE,{"disambiguationData":[OSD([sQuery(id+"F19.wireOp",EDGE,"E44.bottom"),sQuery(id+"F19.wireOp",EDGE,"E44.right")])]});
            var Q1;
            Q1=makeQuery(id+"F20.opExtrude","SWEPT_EDGE",EDGE,{"disambiguationData":[OSD([sQuery(id+"F19.wireOp",EDGE,"E44.top"),sQuery(id+"F19.wireOp",EDGE,"E44.right")])]});
            fillet(context, id + "F26", {"entities" : qUnion([Q0, Q1]), "radius" : 1.9 * mm, "tangentPropagation" : true, "allowEdgeOverflow" : false});
        }
    });